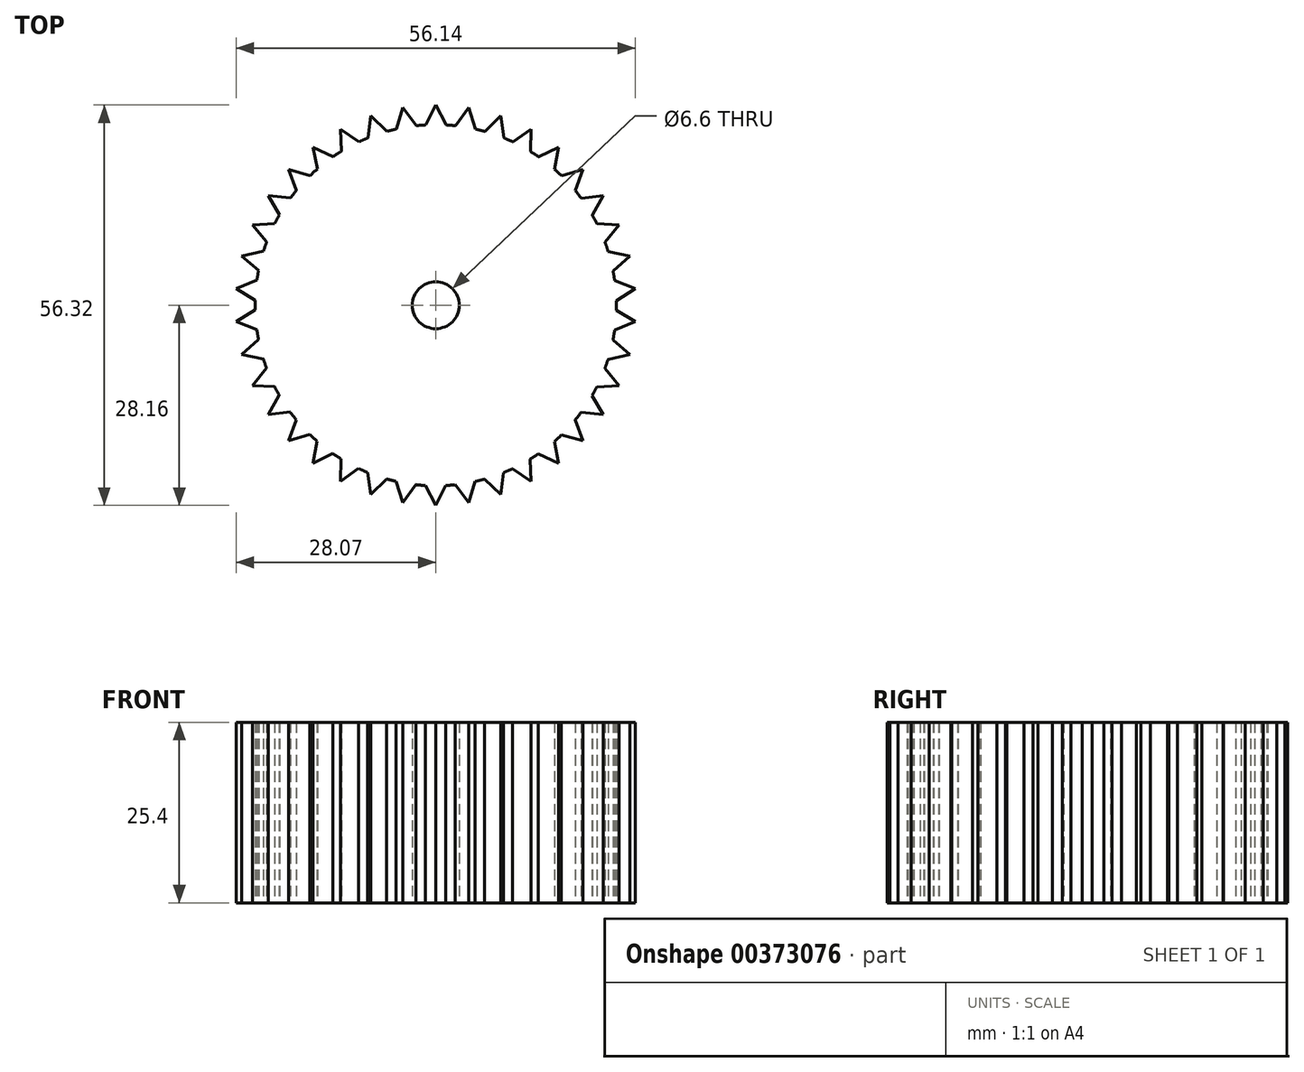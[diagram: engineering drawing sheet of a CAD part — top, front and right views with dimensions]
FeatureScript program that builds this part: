
annotation { "Feature Type Name" : "Feature", "Feature Type Description" : "" }
export const myFeature = defineFeature(function(context is Context, id is Id, definition is map)
    precondition{}
    {
        {
            var Q0;
            Q0=qCreatedBy(makeId("Top.planeOp"),FACE);
            var sketch = newSketch(context, id + "F0", { "sketchPlane" : qUnion([Q0])});
            skCircle(sketch, "E0", {"center": v(0, 0) * mm, "radius": 25.4 * mm});
            skCircle(sketch, "E1", {"center": v(0, 0) * mm, "radius": 3.3 * mm});
            skLineSegment(sketch, "E2", {"start": v(0, 25.4) * mm, "end": v(0, 28.16) * mm});
            skLineSegment(sketch, "E3", {"start": v(0, 28.16) * mm, "end": v(1.44, 25.36) * mm});
            skLineSegment(sketch, "E4", {"start": v(0, 28.16) * mm, "end": v(-1.38, 25.36) * mm});
            skLineSegment(sketch, "E5.1.0", {"start": v(-4.18, 25.05) * mm, "end": v(-4.64, 27.78) * mm});
            skLineSegment(sketch, "E5.1.1", {"start": v(-4.64, 27.78) * mm, "end": v(-5.54, 24.79) * mm});
            skLineSegment(sketch, "E5.1.2", {"start": v(-4.64, 27.78) * mm, "end": v(-2.75, 25.25) * mm});
            skLineSegment(sketch, "E5.2.0", {"start": v(-8.25, 24.02) * mm, "end": v(-9.15, 26.64) * mm});
            skLineSegment(sketch, "E5.2.1", {"start": v(-9.15, 26.64) * mm, "end": v(-9.54, 23.54) * mm});
            skLineSegment(sketch, "E5.2.2", {"start": v(-9.15, 26.64) * mm, "end": v(-6.87, 24.45) * mm});
            skLineSegment(sketch, "E5.3.0", {"start": v(-12.09, 22.34) * mm, "end": v(-13.4, 24.77) * mm});
            skLineSegment(sketch, "E5.3.1", {"start": v(-13.4, 24.77) * mm, "end": v(-13.29, 21.65) * mm});
            skLineSegment(sketch, "E5.3.2", {"start": v(-13.4, 24.77) * mm, "end": v(-10.8, 22.99) * mm});
            skLineSegment(sketch, "E5.4.0", {"start": v(-15.6, 20.04) * mm, "end": v(-17.3, 22.23) * mm});
            skLineSegment(sketch, "E5.4.1", {"start": v(-17.3, 22.23) * mm, "end": v(-16.67, 19.17) * mm});
            skLineSegment(sketch, "E5.4.2", {"start": v(-17.3, 22.23) * mm, "end": v(-14.44, 20.9) * mm});
            skLineSegment(sketch, "E5.5.0", {"start": v(-18.69, 17.2) * mm, "end": v(-20.72, 19.08) * mm});
            skLineSegment(sketch, "E5.5.1", {"start": v(-20.72, 19.08) * mm, "end": v(-19.6, 16.16) * mm});
            skLineSegment(sketch, "E5.5.2", {"start": v(-20.72, 19.08) * mm, "end": v(-17.68, 18.24) * mm});
            skLineSegment(sketch, "E5.6.0", {"start": v(-21.26, 13.9) * mm, "end": v(-23.58, 15.4) * mm});
            skLineSegment(sketch, "E5.6.1", {"start": v(-23.58, 15.4) * mm, "end": v(-21.99, 12.72) * mm});
            skLineSegment(sketch, "E5.6.2", {"start": v(-23.58, 15.4) * mm, "end": v(-20.44, 15.08) * mm});
            skLineSegment(sketch, "E5.7.0", {"start": v(-23.26, 10.2) * mm, "end": v(-25.8, 11.31) * mm});
            skLineSegment(sketch, "E5.7.1", {"start": v(-25.8, 11.31) * mm, "end": v(-23.78, 8.92) * mm});
            skLineSegment(sketch, "E5.7.2", {"start": v(-25.8, 11.31) * mm, "end": v(-22.64, 11.5) * mm});
            skLineSegment(sketch, "E5.8.0", {"start": v(-24.62, 6.24) * mm, "end": v(-27.3, 6.91) * mm});
            skLineSegment(sketch, "E5.8.1", {"start": v(-27.3, 6.91) * mm, "end": v(-24.93, 4.89) * mm});
            skLineSegment(sketch, "E5.8.2", {"start": v(-27.3, 6.91) * mm, "end": v(-24.23, 7.62) * mm});
            skLineSegment(sketch, "E5.9.0", {"start": v(-25.31, 2.1) * mm, "end": v(-28.07, 2.33) * mm});
            skLineSegment(sketch, "E5.9.1", {"start": v(-28.07, 2.33) * mm, "end": v(-25.39, 0.72) * mm});
            skLineSegment(sketch, "E5.9.2", {"start": v(-28.07, 2.33) * mm, "end": v(-25.15, 3.53) * mm});
            skLineSegment(sketch, "E5.10.0", {"start": v(-25.31, -2.1) * mm, "end": v(-28.07, -2.33) * mm});
            skLineSegment(sketch, "E5.10.1", {"start": v(-28.07, -2.33) * mm, "end": v(-25.16, -3.47) * mm});
            skLineSegment(sketch, "E5.10.2", {"start": v(-28.07, -2.33) * mm, "end": v(-25.4, -0.66) * mm});
            skLineSegment(sketch, "E5.11.0", {"start": v(-24.62, -6.24) * mm, "end": v(-27.3, -6.91) * mm});
            skLineSegment(sketch, "E5.11.1", {"start": v(-27.3, -6.91) * mm, "end": v(-24.25, -7.56) * mm});
            skLineSegment(sketch, "E5.11.2", {"start": v(-27.3, -6.91) * mm, "end": v(-24.94, -4.83) * mm});
            skLineSegment(sketch, "E5.12.0", {"start": v(-23.26, -10.2) * mm, "end": v(-25.8, -11.31) * mm});
            skLineSegment(sketch, "E5.12.1", {"start": v(-25.8, -11.31) * mm, "end": v(-22.67, -11.45) * mm});
            skLineSegment(sketch, "E5.12.2", {"start": v(-25.8, -11.31) * mm, "end": v(-23.8, -8.87) * mm});
            skLineSegment(sketch, "E5.13.0", {"start": v(-21.26, -13.9) * mm, "end": v(-23.58, -15.4) * mm});
            skLineSegment(sketch, "E5.13.1", {"start": v(-23.58, -15.4) * mm, "end": v(-20.48, -15.03) * mm});
            skLineSegment(sketch, "E5.13.2", {"start": v(-23.58, -15.4) * mm, "end": v(-22.02, -12.66) * mm});
            skLineSegment(sketch, "E5.14.0", {"start": v(-18.69, -17.2) * mm, "end": v(-20.72, -19.08) * mm});
            skLineSegment(sketch, "E5.14.1", {"start": v(-20.72, -19.08) * mm, "end": v(-17.72, -18.2) * mm});
            skLineSegment(sketch, "E5.14.2", {"start": v(-20.72, -19.08) * mm, "end": v(-19.63, -16.11) * mm});
            skLineSegment(sketch, "E5.15.0", {"start": v(-15.6, -20.04) * mm, "end": v(-17.3, -22.23) * mm});
            skLineSegment(sketch, "E5.15.1", {"start": v(-17.3, -22.23) * mm, "end": v(-14.49, -20.86) * mm});
            skLineSegment(sketch, "E5.15.2", {"start": v(-17.3, -22.23) * mm, "end": v(-16.71, -19.13) * mm});
            skLineSegment(sketch, "E5.16.0", {"start": v(-12.09, -22.34) * mm, "end": v(-13.4, -24.77) * mm});
            skLineSegment(sketch, "E5.16.1", {"start": v(-13.4, -24.77) * mm, "end": v(-10.86, -22.96) * mm});
            skLineSegment(sketch, "E5.16.2", {"start": v(-13.4, -24.77) * mm, "end": v(-13.34, -21.62) * mm});
            skLineSegment(sketch, "E5.17.0", {"start": v(-8.25, -24.02) * mm, "end": v(-9.15, -26.64) * mm});
            skLineSegment(sketch, "E5.17.1", {"start": v(-9.15, -26.64) * mm, "end": v(-6.93, -24.44) * mm});
            skLineSegment(sketch, "E5.17.2", {"start": v(-9.15, -26.64) * mm, "end": v(-9.6, -23.52) * mm});
            skLineSegment(sketch, "E5.18.0", {"start": v(-4.18, -25.05) * mm, "end": v(-4.64, -27.78) * mm});
            skLineSegment(sketch, "E5.18.1", {"start": v(-4.64, -27.78) * mm, "end": v(-2.81, -25.24) * mm});
            skLineSegment(sketch, "E5.18.2", {"start": v(-4.64, -27.78) * mm, "end": v(-5.6, -24.78) * mm});
            skLineSegment(sketch, "E5.19.0", {"start": v(0, -25.4) * mm, "end": v(0, -28.16) * mm});
            skLineSegment(sketch, "E5.19.1", {"start": v(0, -28.16) * mm, "end": v(1.38, -25.36) * mm});
            skLineSegment(sketch, "E5.19.2", {"start": v(0, -28.16) * mm, "end": v(-1.44, -25.36) * mm});
            skLineSegment(sketch, "E5.20.0", {"start": v(4.18, -25.05) * mm, "end": v(4.64, -27.78) * mm});
            skLineSegment(sketch, "E5.20.1", {"start": v(4.64, -27.78) * mm, "end": v(5.54, -24.79) * mm});
            skLineSegment(sketch, "E5.20.2", {"start": v(4.64, -27.78) * mm, "end": v(2.75, -25.25) * mm});
            skLineSegment(sketch, "E5.21.0", {"start": v(8.25, -24.02) * mm, "end": v(9.15, -26.64) * mm});
            skLineSegment(sketch, "E5.21.1", {"start": v(9.15, -26.64) * mm, "end": v(9.54, -23.54) * mm});
            skLineSegment(sketch, "E5.21.2", {"start": v(9.15, -26.64) * mm, "end": v(6.87, -24.45) * mm});
            skLineSegment(sketch, "E5.22.0", {"start": v(12.09, -22.34) * mm, "end": v(13.4, -24.77) * mm});
            skLineSegment(sketch, "E5.22.1", {"start": v(13.4, -24.77) * mm, "end": v(13.29, -21.65) * mm});
            skLineSegment(sketch, "E5.22.2", {"start": v(13.4, -24.77) * mm, "end": v(10.8, -22.99) * mm});
            skLineSegment(sketch, "E5.23.0", {"start": v(15.6, -20.04) * mm, "end": v(17.3, -22.23) * mm});
            skLineSegment(sketch, "E5.23.1", {"start": v(17.3, -22.23) * mm, "end": v(16.67, -19.17) * mm});
            skLineSegment(sketch, "E5.23.2", {"start": v(17.3, -22.23) * mm, "end": v(14.44, -20.9) * mm});
            skLineSegment(sketch, "E5.24.0", {"start": v(18.69, -17.2) * mm, "end": v(20.72, -19.08) * mm});
            skLineSegment(sketch, "E5.24.1", {"start": v(20.72, -19.08) * mm, "end": v(19.6, -16.16) * mm});
            skLineSegment(sketch, "E5.24.2", {"start": v(20.72, -19.08) * mm, "end": v(17.68, -18.24) * mm});
            skLineSegment(sketch, "E5.25.0", {"start": v(21.26, -13.9) * mm, "end": v(23.58, -15.4) * mm});
            skLineSegment(sketch, "E5.25.1", {"start": v(23.58, -15.4) * mm, "end": v(21.99, -12.72) * mm});
            skLineSegment(sketch, "E5.25.2", {"start": v(23.58, -15.4) * mm, "end": v(20.44, -15.08) * mm});
            skLineSegment(sketch, "E5.26.0", {"start": v(23.26, -10.2) * mm, "end": v(25.8, -11.31) * mm});
            skLineSegment(sketch, "E5.26.1", {"start": v(25.8, -11.31) * mm, "end": v(23.78, -8.92) * mm});
            skLineSegment(sketch, "E5.26.2", {"start": v(25.8, -11.31) * mm, "end": v(22.64, -11.5) * mm});
            skLineSegment(sketch, "E5.27.0", {"start": v(24.62, -6.24) * mm, "end": v(27.3, -6.91) * mm});
            skLineSegment(sketch, "E5.27.1", {"start": v(27.3, -6.91) * mm, "end": v(24.93, -4.89) * mm});
            skLineSegment(sketch, "E5.27.2", {"start": v(27.3, -6.91) * mm, "end": v(24.23, -7.62) * mm});
            skLineSegment(sketch, "E5.28.0", {"start": v(25.31, -2.1) * mm, "end": v(28.07, -2.33) * mm});
            skLineSegment(sketch, "E5.28.1", {"start": v(28.07, -2.33) * mm, "end": v(25.39, -0.72) * mm});
            skLineSegment(sketch, "E5.28.2", {"start": v(28.07, -2.33) * mm, "end": v(25.15, -3.53) * mm});
            skLineSegment(sketch, "E5.29.0", {"start": v(25.31, 2.1) * mm, "end": v(28.07, 2.33) * mm});
            skLineSegment(sketch, "E5.29.1", {"start": v(28.07, 2.33) * mm, "end": v(25.16, 3.47) * mm});
            skLineSegment(sketch, "E5.29.2", {"start": v(28.07, 2.33) * mm, "end": v(25.4, 0.66) * mm});
            skLineSegment(sketch, "E5.30.0", {"start": v(24.62, 6.24) * mm, "end": v(27.3, 6.91) * mm});
            skLineSegment(sketch, "E5.30.1", {"start": v(27.3, 6.91) * mm, "end": v(24.25, 7.56) * mm});
            skLineSegment(sketch, "E5.30.2", {"start": v(27.3, 6.91) * mm, "end": v(24.94, 4.83) * mm});
            skLineSegment(sketch, "E5.31.0", {"start": v(23.26, 10.2) * mm, "end": v(25.8, 11.31) * mm});
            skLineSegment(sketch, "E5.31.1", {"start": v(25.8, 11.31) * mm, "end": v(22.67, 11.45) * mm});
            skLineSegment(sketch, "E5.31.2", {"start": v(25.8, 11.31) * mm, "end": v(23.8, 8.87) * mm});
            skLineSegment(sketch, "E5.32.0", {"start": v(21.26, 13.9) * mm, "end": v(23.58, 15.4) * mm});
            skLineSegment(sketch, "E5.32.1", {"start": v(23.58, 15.4) * mm, "end": v(20.48, 15.03) * mm});
            skLineSegment(sketch, "E5.32.2", {"start": v(23.58, 15.4) * mm, "end": v(22.02, 12.66) * mm});
            skLineSegment(sketch, "E5.33.0", {"start": v(18.69, 17.2) * mm, "end": v(20.72, 19.08) * mm});
            skLineSegment(sketch, "E5.33.1", {"start": v(20.72, 19.08) * mm, "end": v(17.72, 18.2) * mm});
            skLineSegment(sketch, "E5.33.2", {"start": v(20.72, 19.08) * mm, "end": v(19.63, 16.11) * mm});
            skLineSegment(sketch, "E5.34.0", {"start": v(15.6, 20.04) * mm, "end": v(17.3, 22.23) * mm});
            skLineSegment(sketch, "E5.34.1", {"start": v(17.3, 22.23) * mm, "end": v(14.49, 20.86) * mm});
            skLineSegment(sketch, "E5.34.2", {"start": v(17.3, 22.23) * mm, "end": v(16.71, 19.13) * mm});
            skLineSegment(sketch, "E5.35.0", {"start": v(12.09, 22.34) * mm, "end": v(13.4, 24.77) * mm});
            skLineSegment(sketch, "E5.35.1", {"start": v(13.4, 24.77) * mm, "end": v(10.86, 22.96) * mm});
            skLineSegment(sketch, "E5.35.2", {"start": v(13.4, 24.77) * mm, "end": v(13.34, 21.62) * mm});
            skLineSegment(sketch, "E5.36.0", {"start": v(8.25, 24.02) * mm, "end": v(9.15, 26.64) * mm});
            skLineSegment(sketch, "E5.36.1", {"start": v(9.15, 26.64) * mm, "end": v(6.93, 24.44) * mm});
            skLineSegment(sketch, "E5.36.2", {"start": v(9.15, 26.64) * mm, "end": v(9.6, 23.52) * mm});
            skLineSegment(sketch, "E5.37.0", {"start": v(4.18, 25.05) * mm, "end": v(4.64, 27.78) * mm});
            skLineSegment(sketch, "E5.37.1", {"start": v(4.64, 27.78) * mm, "end": v(2.81, 25.24) * mm});
            skLineSegment(sketch, "E5.37.2", {"start": v(4.64, 27.78) * mm, "end": v(5.6, 24.78) * mm});
            skSolve(sketch);
        }
        {
            var Q0;
            {var subQ0=sQuery(id+"F0.wireOp",EDGE,"E5.12.0");Q0=makeQuery(id+"F0.imprint","IMPRINT",FACE,{"disambiguationData":[TD([[makeQuery(id+"F0.imprint","IMPRINT",EDGE,{"derivedFrom":subQ0}),1.0]])]});}
            var Q1;
            {var subQ0=sQuery(id+"F0.wireOp",EDGE,"E5.7.0");Q1=makeQuery(id+"F0.imprint","IMPRINT",FACE,{"disambiguationData":[TD([[makeQuery(id+"F0.imprint","IMPRINT",EDGE,{"derivedFrom":subQ0}),-1.0]])]});}
            var Q2;
            {var subQ0=sQuery(id+"F0.wireOp",EDGE,"E5.11.0");Q2=makeQuery(id+"F0.imprint","IMPRINT",FACE,{"disambiguationData":[TD([[makeQuery(id+"F0.imprint","IMPRINT",EDGE,{"derivedFrom":subQ0}),1.0]])]});}
            var Q3;
            {var subQ0=sQuery(id+"F0.wireOp",EDGE,"E5.3.0");Q3=makeQuery(id+"F0.imprint","IMPRINT",FACE,{"disambiguationData":[TD([[makeQuery(id+"F0.imprint","IMPRINT",EDGE,{"derivedFrom":subQ0}),1.0]])]});}
            var Q4;
            {var subQ0=sQuery(id+"F0.wireOp",EDGE,"E5.27.0");Q4=makeQuery(id+"F0.imprint","IMPRINT",FACE,{"disambiguationData":[TD([[makeQuery(id+"F0.imprint","IMPRINT",EDGE,{"derivedFrom":subQ0}),1.0]])]});}
            var Q5;
            {var subQ0=sQuery(id+"F0.wireOp",EDGE,"E5.21.0");Q5=makeQuery(id+"F0.imprint","IMPRINT",FACE,{"disambiguationData":[TD([[makeQuery(id+"F0.imprint","IMPRINT",EDGE,{"derivedFrom":subQ0}),-1.0]])]});}
            var Q6;
            {var subQ0=sQuery(id+"F0.wireOp",EDGE,"E5.13.0");Q6=makeQuery(id+"F0.imprint","IMPRINT",FACE,{"disambiguationData":[TD([[makeQuery(id+"F0.imprint","IMPRINT",EDGE,{"derivedFrom":subQ0}),-1.0]])]});}
            var Q7;
            {var subQ0=sQuery(id+"F0.wireOp",EDGE,"E5.5.0");Q7=makeQuery(id+"F0.imprint","IMPRINT",FACE,{"disambiguationData":[TD([[makeQuery(id+"F0.imprint","IMPRINT",EDGE,{"derivedFrom":subQ0}),-1.0]])]});}
            var Q8;
            {var subQ0=sQuery(id+"F0.wireOp",EDGE,"E5.20.0");Q8=makeQuery(id+"F0.imprint","IMPRINT",FACE,{"disambiguationData":[TD([[makeQuery(id+"F0.imprint","IMPRINT",EDGE,{"derivedFrom":subQ0}),-1.0]])]});}
            var Q9;
            {var subQ0=sQuery(id+"F0.wireOp",EDGE,"E5.12.0");Q9=makeQuery(id+"F0.imprint","IMPRINT",FACE,{"disambiguationData":[TD([[makeQuery(id+"F0.imprint","IMPRINT",EDGE,{"derivedFrom":subQ0}),-1.0]])]});}
            var Q10;
            {var subQ0=sQuery(id+"F0.wireOp",EDGE,"E5.4.0");Q10=makeQuery(id+"F0.imprint","IMPRINT",FACE,{"disambiguationData":[TD([[makeQuery(id+"F0.imprint","IMPRINT",EDGE,{"derivedFrom":subQ0}),-1.0]])]});}
            var Q11;
            {var subQ0=sQuery(id+"F0.wireOp",EDGE,"E5.21.0");Q11=makeQuery(id+"F0.imprint","IMPRINT",FACE,{"disambiguationData":[TD([[makeQuery(id+"F0.imprint","IMPRINT",EDGE,{"derivedFrom":subQ0}),1.0]])]});}
            var Q12;
            {var subQ0=sQuery(id+"F0.wireOp",EDGE,"E5.13.0");Q12=makeQuery(id+"F0.imprint","IMPRINT",FACE,{"disambiguationData":[TD([[makeQuery(id+"F0.imprint","IMPRINT",EDGE,{"derivedFrom":subQ0}),1.0]])]});}
            var Q13;
            {var subQ0=sQuery(id+"F0.wireOp",EDGE,"E5.5.0");Q13=makeQuery(id+"F0.imprint","IMPRINT",FACE,{"disambiguationData":[TD([[makeQuery(id+"F0.imprint","IMPRINT",EDGE,{"derivedFrom":subQ0}),1.0]])]});}
            var Q14;
            {var subQ0=sQuery(id+"F0.wireOp",EDGE,"E5.20.0");Q14=makeQuery(id+"F0.imprint","IMPRINT",FACE,{"disambiguationData":[TD([[makeQuery(id+"F0.imprint","IMPRINT",EDGE,{"derivedFrom":subQ0}),1.0]])]});}
            var Q15;
            {var subQ0=sQuery(id+"F0.wireOp",EDGE,"E5.4.0");Q15=makeQuery(id+"F0.imprint","IMPRINT",FACE,{"disambiguationData":[TD([[makeQuery(id+"F0.imprint","IMPRINT",EDGE,{"derivedFrom":subQ0}),1.0]])]});}
            var Q16;
            {var subQ0=sQuery(id+"F0.wireOp",EDGE,"E5.28.0");Q16=makeQuery(id+"F0.imprint","IMPRINT",FACE,{"disambiguationData":[TD([[makeQuery(id+"F0.imprint","IMPRINT",EDGE,{"derivedFrom":subQ0}),1.0]])]});}
            var Q17;
            {var subQ0=sQuery(id+"F0.wireOp",EDGE,"E5.36.0");Q17=makeQuery(id+"F0.imprint","IMPRINT",FACE,{"disambiguationData":[TD([[makeQuery(id+"F0.imprint","IMPRINT",EDGE,{"derivedFrom":subQ0}),1.0]])]});}
            var Q18;
            {var subQ0=sQuery(id+"F0.wireOp",EDGE,"E5.22.0");Q18=makeQuery(id+"F0.imprint","IMPRINT",FACE,{"disambiguationData":[TD([[makeQuery(id+"F0.imprint","IMPRINT",EDGE,{"derivedFrom":subQ0}),1.0]])]});}
            var Q19;
            {var subQ0=sQuery(id+"F0.wireOp",EDGE,"E5.14.0");Q19=makeQuery(id+"F0.imprint","IMPRINT",FACE,{"disambiguationData":[TD([[makeQuery(id+"F0.imprint","IMPRINT",EDGE,{"derivedFrom":subQ0}),1.0]])]});}
            var Q20;
            {var subQ0=sQuery(id+"F0.wireOp",EDGE,"E5.6.0");Q20=makeQuery(id+"F0.imprint","IMPRINT",FACE,{"disambiguationData":[TD([[makeQuery(id+"F0.imprint","IMPRINT",EDGE,{"derivedFrom":subQ0}),1.0]])]});}
            var Q21;
            {var subQ0=sQuery(id+"F0.wireOp",EDGE,"E5.37.0");Q21=makeQuery(id+"F0.imprint","IMPRINT",FACE,{"disambiguationData":[TD([[makeQuery(id+"F0.imprint","IMPRINT",EDGE,{"derivedFrom":subQ0}),-1.0]])]});}
            var Q22;
            {var subQ0=sQuery(id+"F0.wireOp",EDGE,"E5.15.0");Q22=makeQuery(id+"F0.imprint","IMPRINT",FACE,{"disambiguationData":[TD([[makeQuery(id+"F0.imprint","IMPRINT",EDGE,{"derivedFrom":subQ0}),-1.0]])]});}
            var Q23;
            {var subQ0=sQuery(id+"F0.wireOp",EDGE,"E5.37.0");Q23=makeQuery(id+"F0.imprint","IMPRINT",FACE,{"disambiguationData":[TD([[makeQuery(id+"F0.imprint","IMPRINT",EDGE,{"derivedFrom":subQ0}),1.0]])]});}
            var Q24;
            {var subQ0=sQuery(id+"F0.wireOp",EDGE,"E5.23.0");Q24=makeQuery(id+"F0.imprint","IMPRINT",FACE,{"disambiguationData":[TD([[makeQuery(id+"F0.imprint","IMPRINT",EDGE,{"derivedFrom":subQ0}),1.0]])]});}
            var Q25;
            {var subQ0=sQuery(id+"F0.wireOp",EDGE,"E5.15.0");Q25=makeQuery(id+"F0.imprint","IMPRINT",FACE,{"disambiguationData":[TD([[makeQuery(id+"F0.imprint","IMPRINT",EDGE,{"derivedFrom":subQ0}),1.0]])]});}
            var Q26;
            {var subQ0=sQuery(id+"F0.wireOp",EDGE,"E5.7.0");Q26=makeQuery(id+"F0.imprint","IMPRINT",FACE,{"disambiguationData":[TD([[makeQuery(id+"F0.imprint","IMPRINT",EDGE,{"derivedFrom":subQ0}),1.0]])]});}
            var Q27;
            {var subQ0=sQuery(id+"F0.wireOp",EDGE,"E5.24.0");Q27=makeQuery(id+"F0.imprint","IMPRINT",FACE,{"disambiguationData":[TD([[makeQuery(id+"F0.imprint","IMPRINT",EDGE,{"derivedFrom":subQ0}),-1.0]])]});}
            var Q28;
            {var subQ0=sQuery(id+"F0.wireOp",EDGE,"E5.16.0");Q28=makeQuery(id+"F0.imprint","IMPRINT",FACE,{"disambiguationData":[TD([[makeQuery(id+"F0.imprint","IMPRINT",EDGE,{"derivedFrom":subQ0}),-1.0]])]});}
            var Q29;
            {var subQ0=sQuery(id+"F0.wireOp",EDGE,"E5.8.0");Q29=makeQuery(id+"F0.imprint","IMPRINT",FACE,{"disambiguationData":[TD([[makeQuery(id+"F0.imprint","IMPRINT",EDGE,{"derivedFrom":subQ0}),-1.0]])]});}
            var Q30;
            {var subQ0=sQuery(id+"F0.wireOp",EDGE,"E2");Q30=makeQuery(id+"F0.imprint","IMPRINT",FACE,{"disambiguationData":[TD([[makeQuery(id+"F0.imprint","IMPRINT",EDGE,{"derivedFrom":subQ0}),1.0]])]});}
            var Q31;
            {var subQ0=sQuery(id+"F0.wireOp",EDGE,"E5.24.0");Q31=makeQuery(id+"F0.imprint","IMPRINT",FACE,{"disambiguationData":[TD([[makeQuery(id+"F0.imprint","IMPRINT",EDGE,{"derivedFrom":subQ0}),1.0]])]});}
            var Q32;
            {var subQ0=sQuery(id+"F0.wireOp",EDGE,"E5.16.0");Q32=makeQuery(id+"F0.imprint","IMPRINT",FACE,{"disambiguationData":[TD([[makeQuery(id+"F0.imprint","IMPRINT",EDGE,{"derivedFrom":subQ0}),1.0]])]});}
            var Q33;
            {var subQ0=sQuery(id+"F0.wireOp",EDGE,"E5.8.0");Q33=makeQuery(id+"F0.imprint","IMPRINT",FACE,{"disambiguationData":[TD([[makeQuery(id+"F0.imprint","IMPRINT",EDGE,{"derivedFrom":subQ0}),1.0]])]});}
            var Q34;
            {var subQ0=sQuery(id+"F0.wireOp",EDGE,"E5.1.0");Q34=makeQuery(id+"F0.imprint","IMPRINT",FACE,{"disambiguationData":[TD([[makeQuery(id+"F0.imprint","IMPRINT",EDGE,{"derivedFrom":subQ0}),-1.0]])]});}
            var Q35;
            {var subQ0=sQuery(id+"F0.wireOp",EDGE,"E5.25.0");Q35=makeQuery(id+"F0.imprint","IMPRINT",FACE,{"disambiguationData":[TD([[makeQuery(id+"F0.imprint","IMPRINT",EDGE,{"derivedFrom":subQ0}),-1.0]])]});}
            var Q36;
            {var subQ0=sQuery(id+"F0.wireOp",EDGE,"E5.17.0");Q36=makeQuery(id+"F0.imprint","IMPRINT",FACE,{"disambiguationData":[TD([[makeQuery(id+"F0.imprint","IMPRINT",EDGE,{"derivedFrom":subQ0}),-1.0]])]});}
            var Q37;
            {var subQ0=sQuery(id+"F0.wireOp",EDGE,"E5.25.0");Q37=makeQuery(id+"F0.imprint","IMPRINT",FACE,{"disambiguationData":[TD([[makeQuery(id+"F0.imprint","IMPRINT",EDGE,{"derivedFrom":subQ0}),1.0]])]});}
            var Q38;
            {var subQ0=sQuery(id+"F0.wireOp",EDGE,"E5.17.0");Q38=makeQuery(id+"F0.imprint","IMPRINT",FACE,{"disambiguationData":[TD([[makeQuery(id+"F0.imprint","IMPRINT",EDGE,{"derivedFrom":subQ0}),1.0]])]});}
            var Q39;
            {var subQ0=sQuery(id+"F0.wireOp",EDGE,"E5.9.0");Q39=makeQuery(id+"F0.imprint","IMPRINT",FACE,{"disambiguationData":[TD([[makeQuery(id+"F0.imprint","IMPRINT",EDGE,{"derivedFrom":subQ0}),1.0]])]});}
            var Q40;
            {var subQ0=sQuery(id+"F0.wireOp",EDGE,"E5.1.0");Q40=makeQuery(id+"F0.imprint","IMPRINT",FACE,{"disambiguationData":[TD([[makeQuery(id+"F0.imprint","IMPRINT",EDGE,{"derivedFrom":subQ0}),1.0]])]});}
            var Q41;
            {var subQ0=sQuery(id+"F0.wireOp",EDGE,"E5.36.0");Q41=makeQuery(id+"F0.imprint","IMPRINT",FACE,{"disambiguationData":[TD([[makeQuery(id+"F0.imprint","IMPRINT",EDGE,{"derivedFrom":subQ0}),-1.0]])]});}
            var Q42;
            {var subQ0=sQuery(id+"F0.wireOp",EDGE,"E5.35.0");Q42=makeQuery(id+"F0.imprint","IMPRINT",FACE,{"disambiguationData":[TD([[makeQuery(id+"F0.imprint","IMPRINT",EDGE,{"derivedFrom":subQ0}),-1.0]])]});}
            var Q43;
            {var subQ0=sQuery(id+"F0.wireOp",EDGE,"E5.35.0");Q43=makeQuery(id+"F0.imprint","IMPRINT",FACE,{"disambiguationData":[TD([[makeQuery(id+"F0.imprint","IMPRINT",EDGE,{"derivedFrom":subQ0}),1.0]])]});}
            var Q44;
            {var subQ0=sQuery(id+"F0.wireOp",EDGE,"E5.29.0");Q44=makeQuery(id+"F0.imprint","IMPRINT",FACE,{"disambiguationData":[TD([[makeQuery(id+"F0.imprint","IMPRINT",EDGE,{"derivedFrom":subQ0}),-1.0]])]});}
            var Q45;
            {var subQ0=sQuery(id+"F0.wireOp",EDGE,"E5.29.0");Q45=makeQuery(id+"F0.imprint","IMPRINT",FACE,{"disambiguationData":[TD([[makeQuery(id+"F0.imprint","IMPRINT",EDGE,{"derivedFrom":subQ0}),1.0]])]});}
            var Q46;
            {var subQ0=sQuery(id+"F0.wireOp",EDGE,"E5.30.0");Q46=makeQuery(id+"F0.imprint","IMPRINT",FACE,{"disambiguationData":[TD([[makeQuery(id+"F0.imprint","IMPRINT",EDGE,{"derivedFrom":subQ0}),1.0]])]});}
            var Q47;
            {var subQ0=sQuery(id+"F0.wireOp",EDGE,"E5.31.0");Q47=makeQuery(id+"F0.imprint","IMPRINT",FACE,{"disambiguationData":[TD([[makeQuery(id+"F0.imprint","IMPRINT",EDGE,{"derivedFrom":subQ0}),-1.0]])]});}
            var Q48;
            {var subQ0=sQuery(id+"F0.wireOp",EDGE,"E5.31.0");Q48=makeQuery(id+"F0.imprint","IMPRINT",FACE,{"disambiguationData":[TD([[makeQuery(id+"F0.imprint","IMPRINT",EDGE,{"derivedFrom":subQ0}),1.0]])]});}
            var Q49;
            {var subQ0=sQuery(id+"F0.wireOp",EDGE,"E5.32.0");Q49=makeQuery(id+"F0.imprint","IMPRINT",FACE,{"disambiguationData":[TD([[makeQuery(id+"F0.imprint","IMPRINT",EDGE,{"derivedFrom":subQ0}),-1.0]])]});}
            var Q50;
            {var subQ0=sQuery(id+"F0.wireOp",EDGE,"E5.32.0");Q50=makeQuery(id+"F0.imprint","IMPRINT",FACE,{"disambiguationData":[TD([[makeQuery(id+"F0.imprint","IMPRINT",EDGE,{"derivedFrom":subQ0}),1.0]])]});}
            var Q51;
            {var subQ0=sQuery(id+"F0.wireOp",EDGE,"E5.33.0");Q51=makeQuery(id+"F0.imprint","IMPRINT",FACE,{"disambiguationData":[TD([[makeQuery(id+"F0.imprint","IMPRINT",EDGE,{"derivedFrom":subQ0}),-1.0]])]});}
            var Q52;
            {var subQ0=sQuery(id+"F0.wireOp",EDGE,"E5.33.0");Q52=makeQuery(id+"F0.imprint","IMPRINT",FACE,{"disambiguationData":[TD([[makeQuery(id+"F0.imprint","IMPRINT",EDGE,{"derivedFrom":subQ0}),1.0]])]});}
            var Q53;
            {var subQ0=sQuery(id+"F0.wireOp",EDGE,"E5.34.0");Q53=makeQuery(id+"F0.imprint","IMPRINT",FACE,{"disambiguationData":[TD([[makeQuery(id+"F0.imprint","IMPRINT",EDGE,{"derivedFrom":subQ0}),-1.0]])]});}
            var Q54;
            {var subQ0=sQuery(id+"F0.wireOp",EDGE,"E5.34.0");Q54=makeQuery(id+"F0.imprint","IMPRINT",FACE,{"disambiguationData":[TD([[makeQuery(id+"F0.imprint","IMPRINT",EDGE,{"derivedFrom":subQ0}),1.0]])]});}
            var Q55;
            {var subQ0=sQuery(id+"F0.wireOp",EDGE,"E5.18.0");Q55=makeQuery(id+"F0.imprint","IMPRINT",FACE,{"disambiguationData":[TD([[makeQuery(id+"F0.imprint","IMPRINT",EDGE,{"derivedFrom":subQ0}),-1.0]])]});}
            var Q56;
            {var subQ0=sQuery(id+"F0.wireOp",EDGE,"E5.10.0");Q56=makeQuery(id+"F0.imprint","IMPRINT",FACE,{"disambiguationData":[TD([[makeQuery(id+"F0.imprint","IMPRINT",EDGE,{"derivedFrom":subQ0}),-1.0]])]});}
            var Q57;
            {var subQ0=sQuery(id+"F0.wireOp",EDGE,"E5.2.0");Q57=makeQuery(id+"F0.imprint","IMPRINT",FACE,{"disambiguationData":[TD([[makeQuery(id+"F0.imprint","IMPRINT",EDGE,{"derivedFrom":subQ0}),-1.0]])]});}
            var Q58;
            {var subQ0=sQuery(id+"F0.wireOp",EDGE,"E5.26.0");Q58=makeQuery(id+"F0.imprint","IMPRINT",FACE,{"disambiguationData":[TD([[makeQuery(id+"F0.imprint","IMPRINT",EDGE,{"derivedFrom":subQ0}),-1.0]])]});}
            var Q59;
            {var subQ0=sQuery(id+"F0.wireOp",EDGE,"E5.18.0");Q59=makeQuery(id+"F0.imprint","IMPRINT",FACE,{"disambiguationData":[TD([[makeQuery(id+"F0.imprint","IMPRINT",EDGE,{"derivedFrom":subQ0}),1.0]])]});}
            var Q60;
            {var subQ0=sQuery(id+"F0.wireOp",EDGE,"E5.10.0");Q60=makeQuery(id+"F0.imprint","IMPRINT",FACE,{"disambiguationData":[TD([[makeQuery(id+"F0.imprint","IMPRINT",EDGE,{"derivedFrom":subQ0}),1.0]])]});}
            var Q61;
            {var subQ0=sQuery(id+"F0.wireOp",EDGE,"E5.2.0");Q61=makeQuery(id+"F0.imprint","IMPRINT",FACE,{"disambiguationData":[TD([[makeQuery(id+"F0.imprint","IMPRINT",EDGE,{"derivedFrom":subQ0}),1.0]])]});}
            var Q62;
            {var subQ0=sQuery(id+"F0.wireOp",EDGE,"E5.26.0");Q62=makeQuery(id+"F0.imprint","IMPRINT",FACE,{"disambiguationData":[TD([[makeQuery(id+"F0.imprint","IMPRINT",EDGE,{"derivedFrom":subQ0}),1.0]])]});}
            var Q63;
            {var subQ0=sQuery(id+"F0.wireOp",EDGE,"E5.6.0");Q63=makeQuery(id+"F0.imprint","IMPRINT",FACE,{"disambiguationData":[TD([[makeQuery(id+"F0.imprint","IMPRINT",EDGE,{"derivedFrom":subQ0}),-1.0]])]});}
            var Q64;
            {var subQ0=sQuery(id+"F0.wireOp",EDGE,"E5.11.0");Q64=makeQuery(id+"F0.imprint","IMPRINT",FACE,{"disambiguationData":[TD([[makeQuery(id+"F0.imprint","IMPRINT",EDGE,{"derivedFrom":subQ0}),-1.0]])]});}
            var Q65;
            {var subQ0=sQuery(id+"F0.wireOp",EDGE,"E5.3.0");Q65=makeQuery(id+"F0.imprint","IMPRINT",FACE,{"disambiguationData":[TD([[makeQuery(id+"F0.imprint","IMPRINT",EDGE,{"derivedFrom":subQ0}),-1.0]])]});}
            var Q66;
            {var subQ0=sQuery(id+"F0.wireOp",EDGE,"E5.22.0");Q66=makeQuery(id+"F0.imprint","IMPRINT",FACE,{"disambiguationData":[TD([[makeQuery(id+"F0.imprint","IMPRINT",EDGE,{"derivedFrom":subQ0}),-1.0]])]});}
            var Q67;
            {var subQ0=sQuery(id+"F0.wireOp",EDGE,"E5.14.0");Q67=makeQuery(id+"F0.imprint","IMPRINT",FACE,{"disambiguationData":[TD([[makeQuery(id+"F0.imprint","IMPRINT",EDGE,{"derivedFrom":subQ0}),-1.0]])]});}
            var Q68;
            {var subQ0=sQuery(id+"F0.wireOp",EDGE,"E5.27.0");Q68=makeQuery(id+"F0.imprint","IMPRINT",FACE,{"disambiguationData":[TD([[makeQuery(id+"F0.imprint","IMPRINT",EDGE,{"derivedFrom":subQ0}),-1.0]])]});}
            var Q69;
            {var subQ0=sQuery(id+"F0.wireOp",EDGE,"E5.19.0");Q69=makeQuery(id+"F0.imprint","IMPRINT",FACE,{"disambiguationData":[TD([[makeQuery(id+"F0.imprint","IMPRINT",EDGE,{"derivedFrom":subQ0}),1.0]])]});}
            var Q70;
            {var subQ0=sQuery(id+"F0.wireOp",EDGE,"E5.28.0");Q70=makeQuery(id+"F0.imprint","IMPRINT",FACE,{"disambiguationData":[TD([[makeQuery(id+"F0.imprint","IMPRINT",EDGE,{"derivedFrom":subQ0}),-1.0]])]});}
            var Q71;
            {var subQ0=sQuery(id+"F0.wireOp",EDGE,"E5.23.0");Q71=makeQuery(id+"F0.imprint","IMPRINT",FACE,{"disambiguationData":[TD([[makeQuery(id+"F0.imprint","IMPRINT",EDGE,{"derivedFrom":subQ0}),-1.0]])]});}
            var Q72;
            {var subQ0=sQuery(id+"F0.wireOp",EDGE,"E2");Q72=makeQuery(id+"F0.imprint","IMPRINT",FACE,{"disambiguationData":[TD([[makeQuery(id+"F0.imprint","IMPRINT",EDGE,{"derivedFrom":subQ0}),-1.0]])]});}
            var Q73;
            {var subQ0=sQuery(id+"F0.wireOp",EDGE,"E5.9.0");Q73=makeQuery(id+"F0.imprint","IMPRINT",FACE,{"disambiguationData":[TD([[makeQuery(id+"F0.imprint","IMPRINT",EDGE,{"derivedFrom":subQ0}),-1.0]])]});}
            var Q74;
            {var subQ0=sQuery(id+"F0.wireOp",EDGE,"E5.30.0");Q74=makeQuery(id+"F0.imprint","IMPRINT",FACE,{"disambiguationData":[TD([[makeQuery(id+"F0.imprint","IMPRINT",EDGE,{"derivedFrom":subQ0}),-1.0]])]});}
            var Q75;
            {var subQ0=sQuery(id+"F0.wireOp",EDGE,"E5.19.0");Q75=makeQuery(id+"F0.imprint","IMPRINT",FACE,{"disambiguationData":[TD([[makeQuery(id+"F0.imprint","IMPRINT",EDGE,{"derivedFrom":subQ0}),-1.0]])]});}
            var Q76;
            Q76=makeQuery(id+"F0.imprint","IMPRINT",FACE,{"disambiguationData":[TD([[makeQuery(id+"F0.imprint","IMPRINT",EDGE,{"derivedFrom":sQuery(id+"F0.wireOp",EDGE,"E1")}),-1.0]])]});
            extrude(context, id + "F1", {"entities" : qUnion([Q0, Q1, Q2, Q3, Q4, Q5, Q6, Q7, Q8, Q9, Q10, Q11, Q12, Q13, Q14, Q15, Q16, Q17, Q18, Q19, Q20, Q21, Q22, Q23, Q24, Q25, Q26, Q27, Q28, Q29, Q30, Q31, Q32, Q33, Q34, Q35, Q36, Q37, Q38, Q39, Q40, Q41, Q42, Q43, Q44, Q45, Q46, Q47, Q48, Q49, Q50, Q51, Q52, Q53, Q54, Q55, Q56, Q57, Q58, Q59, Q60, Q61, Q62, Q63, Q64, Q65, Q66, Q67, Q68, Q69, Q70, Q71, Q72, Q73, Q74, Q75, Q76]), "depth" : 25.4 * mm});
        }
    });
